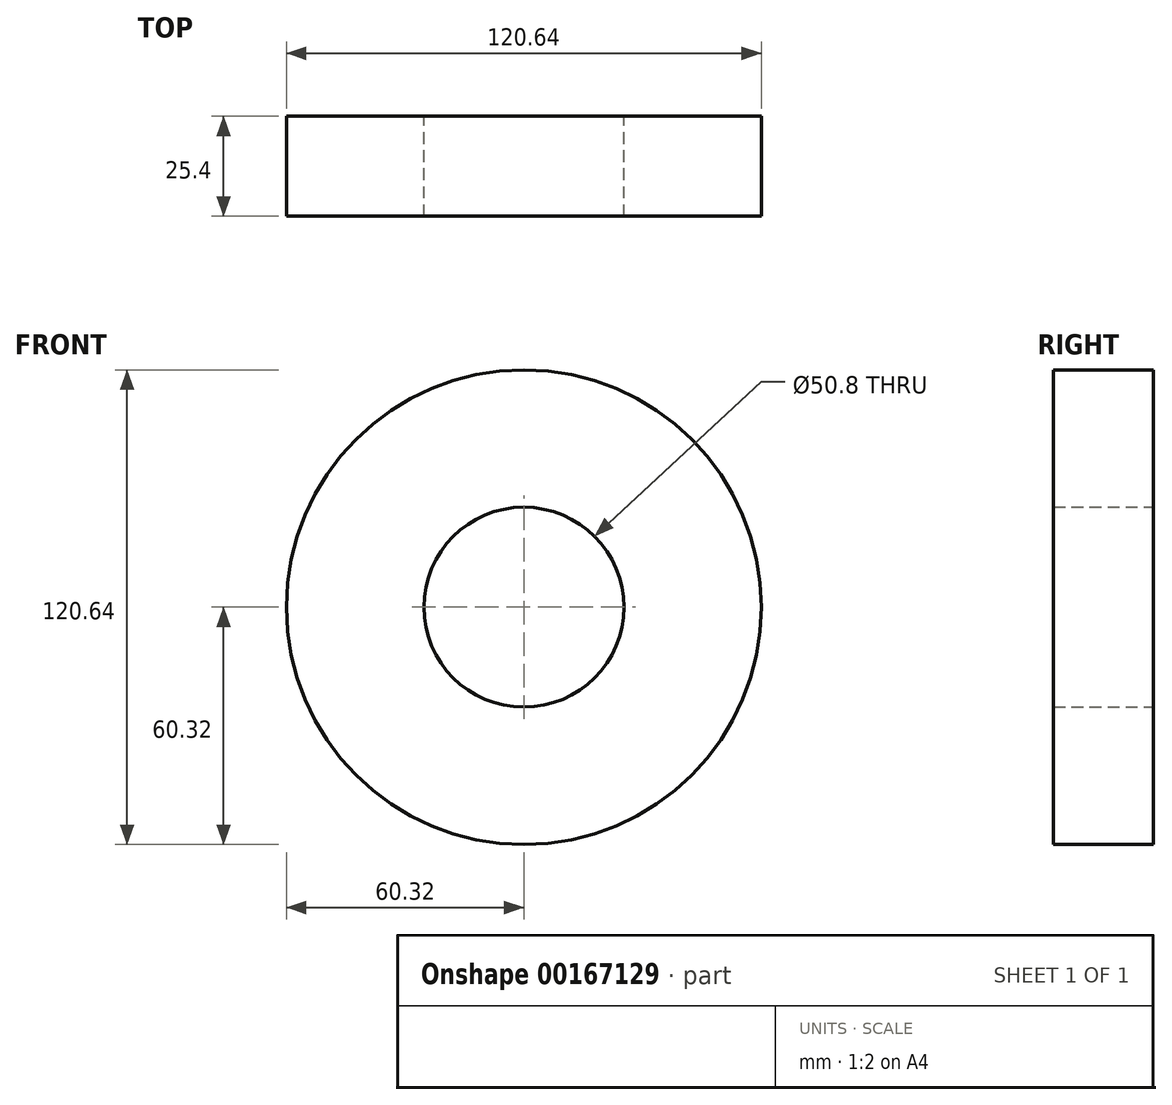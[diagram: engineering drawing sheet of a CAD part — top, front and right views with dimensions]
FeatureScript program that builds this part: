
annotation { "Feature Type Name" : "Feature", "Feature Type Description" : "" }
export const myFeature = defineFeature(function(context is Context, id is Id, definition is map)
    precondition{}
    {
        {
            var Q0;
            Q0=qCreatedBy(makeId("Front.planeOp"),FACE);
            var sketch = newSketch(context, id + "F0", { "sketchPlane" : qUnion([Q0])});
            skCircle(sketch, "E0", {"center": v(0, 0) * mm, "radius": 60.32 * mm});
            skCircle(sketch, "E1", {"center": v(0, 0) * mm, "radius": 25.4 * mm});
            skSolve(sketch);
        }
        {
            var Q0;
            Q0 = qSketchRegion(id + "F0", true);
            extrude(context, id + "F1", {"entities" : qUnion([Q0]), "depth" : 10.16 * mm});
        }
        {
            var Q0;
            Q0=makeQuery(id+"F0.imprint","IMPRINT",FACE,{"disambiguationData":[TD([[makeQuery(id+"F0.imprint","IMPRINT",EDGE,{"derivedFrom":sQuery(id+"F0.wireOp",EDGE,"E0")}),1.0]])]});
            extrude(context, id + "F2", {"entities" : qUnion([Q0]), "operationType" : NewBodyOperationType.ADD, "endBound" : BoundingType.SYMMETRIC, "depth" : 25.4 * mm});
        }
    });
